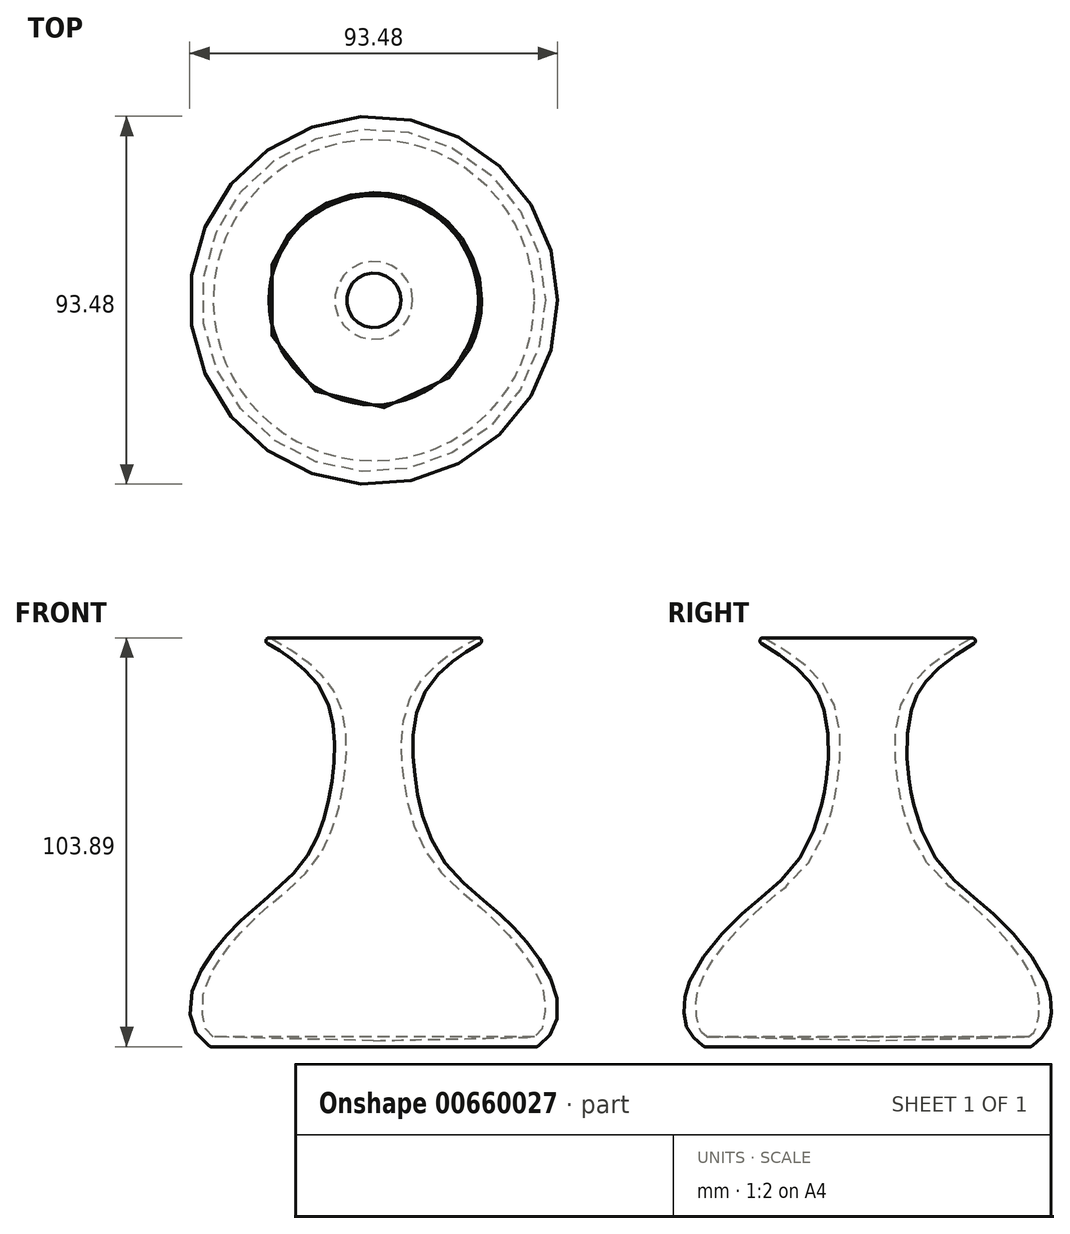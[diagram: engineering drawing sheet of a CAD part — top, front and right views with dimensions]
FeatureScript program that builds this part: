
annotation { "Feature Type Name" : "Feature", "Feature Type Description" : "" }
export const myFeature = defineFeature(function(context is Context, id is Id, definition is map)
    precondition{}
    {
        {
            var Q0;
            Q0=qCreatedBy(makeId("Front.planeOp"),FACE);
            var sketch = newSketch(context, id + "F0", { "sketchPlane" : qUnion([Q0])});
            skFitSpline(sketch, "E0", {"points": [v(-29.57, 43.6) * mm, v(-24.36, 40.57) * mm, v(-19.05, 36.79) * mm, v(-12.66, 29.3) * mm, v(-9.96, 18.02) * mm, v(-10.38, 9) * mm, v(-12, 0) * mm, v(-18.08, -13.58) * mm, v(-29.57, -24.48) * mm, v(-35.92, -30.42) * mm, v(-42, -37.93) * mm, v(-46.4, -47.41) * mm, v(-45.69, -55.9) * mm, v(-41.58, -60.3) * mm], "startDerivative": vector(85.84, -48.25) * mm, "endDerivative": vector(78.73, -65.67) * mm});
            skLineSegment(sketch, "E1", {"start": v(0, 62.86) * mm, "end": v(0, -67.09) * mm});
            skFitSpline(sketch, "E2", {"points": [v(-26.57, 43.6) * mm, v(-21.36, 40.57) * mm, v(-16.05, 36.79) * mm, v(-9.66, 29.3) * mm, v(-6.96, 18.02) * mm, v(-7.38, 9) * mm, v(-9, 0) * mm, v(-15.08, -13.58) * mm, v(-26.57, -24.48) * mm, v(-32.92, -30.42) * mm, v(-39, -37.93) * mm, v(-43.4, -47.41) * mm, v(-42.69, -55.9) * mm, v(-40.8, -57.84) * mm], "startDerivative": vector(85.84, -48.25) * mm, "endDerivative": vector(78.73, -65.67) * mm});
            skFitSpline(sketch, "E3", {"points": [v(-41.58, -60.3) * mm, v(0, -60.3) * mm], "startDerivative": vector(41.58, 0) * mm, "endDerivative": vector(41.58, 0) * mm});
            skLineSegment(sketch, "E4", {"start": v(-40.8, -57.84) * mm, "end": v(0, -58.78) * mm});
            skLineSegment(sketch, "E5", {"start": v(-29.57, 43.6) * mm, "end": v(-26.57, 43.6) * mm});
            skSolve(sketch);
        }
        {
            var Q0;
            Q0=makeQuery(id+"F0.imprint","IMPRINT",FACE,{"disambiguationData":[TD([[makeQuery(id+"F0.imprint","IMPRINT",EDGE,{"derivedFrom":sQuery(id+"F0.wireOp",EDGE,"E0")}),1.0]])]});
            var Q1;
            Q1=sQuery(id+"F0.wireOp",EDGE,"E1");
            revolve(context, id + "F1", {"entities" : qUnion([Q0]), "axis" : qUnion([Q1]), "revolveType" : RevolveType.FULL});
        }
        {
            var Q0;
            Q0=makeQuery(id+"F1.opRevolve","SWEPT_FACE",FACE,{"disambiguationData":[OSD([sQuery(id+"F0.wireOp",EDGE,"E3")])]});
            var Q1;
            Q1=makeQuery(id+"F1.opRevolve","SWEPT_FACE",FACE,{"disambiguationData":[OSD([sQuery(id+"F0.wireOp",EDGE,"E0")])]});
            fillet(context, id + "F2", {"entities" : qUnion([Q0, Q1]), "radius" : 0.78 * mm, "tangentPropagation" : true, "allowEdgeOverflow" : false});
        }
    });
